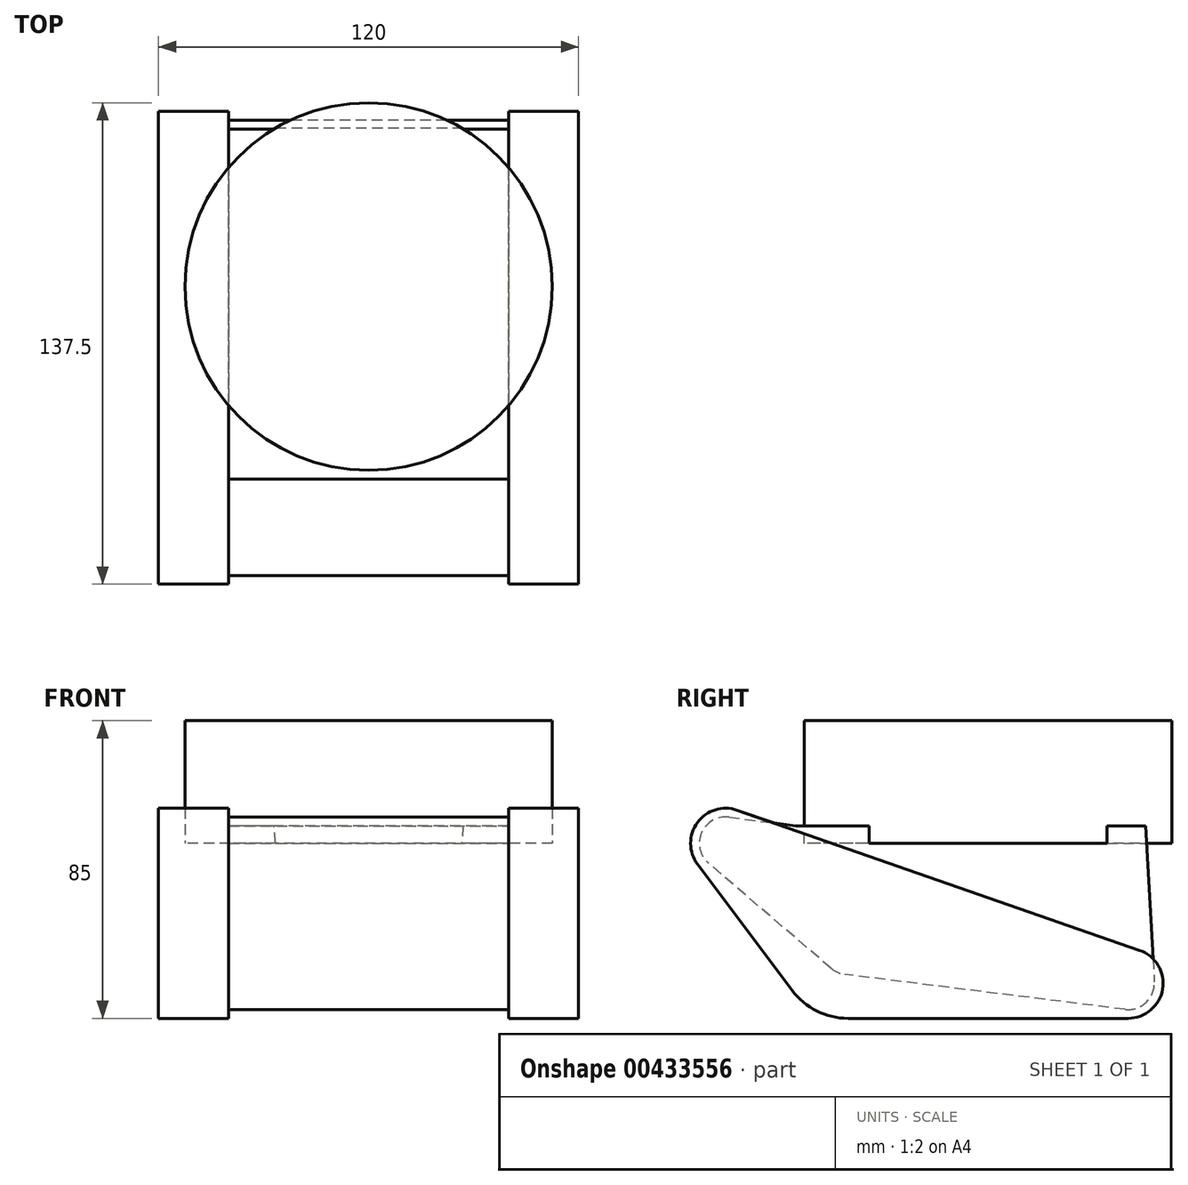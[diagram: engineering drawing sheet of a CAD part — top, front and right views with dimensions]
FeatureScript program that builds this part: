
annotation { "Feature Type Name" : "Feature", "Feature Type Description" : "" }
export const myFeature = defineFeature(function(context is Context, id is Id, definition is map)
    precondition{}
    {
        {
            var Q0;
            Q0=qCreatedBy(makeId("Right.planeOp"),FACE);
            var sketch = newSketch(context, id + "F0", { "sketchPlane" : qUnion([Q0])});
            skLineSegment(sketch, "E0", {"start": v(0, 0) * mm, "end": v(40, 0) * mm, "construction": true});
            skLineSegment(sketch, "E1", {"start": v(0, 0) * mm, "end": v(-40, 0) * mm, "construction": true});
            skLineSegment(sketch, "E2", {"start": v(-40, 0) * mm, "end": v(-40, 10) * mm, "construction": true});
            skCircle(sketch, "E3", {"center": v(40, 0) * mm, "radius": 10 * mm});
            skCircle(sketch, "E4", {"center": v(-40, 10) * mm, "radius": 20 * mm});
            skLineSegment(sketch, "E5", {"start": v(40, -10) * mm, "end": v(-40, -10) * mm});
            skLineSegment(sketch, "E6", {"start": v(-40, 0) * mm, "end": v(-75, 0) * mm, "construction": true});
            skLineSegment(sketch, "E7", {"start": v(-75, 0) * mm, "end": v(-75, 40) * mm, "construction": true});
            skCircle(sketch, "E8", {"center": v(-75, 40) * mm, "radius": 10 * mm});
            skLineSegment(sketch, "E9", {"start": v(-83, 34) * mm, "end": v(-56, -2) * mm});
            skLineSegment(sketch, "E10", {"start": v(-71.71, 49.44) * mm, "end": v(43.29, 9.44) * mm});
            skLineSegment(sketch, "E11", {"start": v(-40, 10) * mm, "end": v(-55, 10) * mm, "construction": true});
            skLineSegment(sketch, "E12", {"start": v(-55, 10) * mm, "end": v(-55, 45) * mm, "construction": true});
            skLineSegment(sketch, "E13", {"start": v(40, 0) * mm, "end": v(45, 0) * mm, "construction": true});
            skLineSegment(sketch, "E14", {"start": v(45, 0) * mm, "end": v(45, 45) * mm, "construction": true});
            skLineSegment(sketch, "E15.bottom", {"start": v(-55, 45) * mm, "end": v(45, 45) * mm});
            skLineSegment(sketch, "E15.top", {"start": v(-55, 75) * mm, "end": v(45, 75) * mm});
            skLineSegment(sketch, "E15.left", {"start": v(-55, 45) * mm, "end": v(-55, 75) * mm});
            skLineSegment(sketch, "E15.right", {"start": v(45, 45) * mm, "end": v(45, 75) * mm});
            skLineSegment(sketch, "E16", {"start": v(-5, 75) * mm, "end": v(-5, 45) * mm, "construction": true});
            skCircle(sketch, "E17", {"center": v(-75, 40) * mm, "radius": 7.5 * mm});
            skCircle(sketch, "E18", {"center": v(-40, 10) * mm, "radius": 7.5 * mm});
            skCircle(sketch, "E19", {"center": v(40, 0) * mm, "radius": 7.5 * mm});
            skLineSegment(sketch, "E20", {"start": v(39.07, -7.44) * mm, "end": v(-40.93, 2.56) * mm});
            skLineSegment(sketch, "E21", {"start": v(-44.88, 4.3) * mm, "end": v(-79.88, 34.3) * mm});
            skLineSegment(sketch, "E22", {"start": v(-74.05, 47.44) * mm, "end": v(-55, 45) * mm});
            skLineSegment(sketch, "E23", {"start": v(45, 45) * mm, "end": v(47.49, 0.42) * mm});
            skSolve(sketch);
        }
        {
            var Q0;
            {var subQ0=sQuery(id+"F0.wireOp",EDGE,"E17");var subQ1=makeQuery(id+"F0.imprint","INTERSECT",VERTEX,{"derivedFrom":[subQ0,sQuery(id+"F0.wireOp",EDGE,"E21")]});Q0=makeQuery(id+"F0.imprint","IMPRINT",FACE,{"disambiguationData":[TD([[makeQuery(id+"F0.imprint","IMPRINT",EDGE,{"disambiguationData":[TD([[subQ1,1.0]])],"derivedFrom":subQ0}),1.0]])]});}
            var Q1;
            {var subQ0=sQuery(id+"F0.wireOp",EDGE,"E10");var subQ1=sQuery(id+"F0.wireOp",EDGE,"E3");var subQ2=makeQuery(id+"F0.imprint","INTERSECT",VERTEX,{"derivedFrom":[subQ1,subQ0]});Q1=makeQuery(id+"F0.imprint","IMPRINT",FACE,{"disambiguationData":[TD([[makeQuery(id+"F0.imprint","IMPRINT",EDGE,{"disambiguationData":[TD([[subQ2,-1.0]])],"derivedFrom":subQ1}),-1.0]])]});}
            var Q2;
            {var subQ0=sQuery(id+"F0.wireOp",EDGE,"E22");var subQ1=sQuery(id+"F0.wireOp",EDGE,"E8");var subQ2=makeQuery(id+"F0.imprint","INTERSECT",VERTEX,{"derivedFrom":[subQ1,subQ0]});Q2=makeQuery(id+"F0.imprint","IMPRINT",FACE,{"disambiguationData":[TD([[makeQuery(id+"F0.imprint","IMPRINT",EDGE,{"disambiguationData":[TD([[subQ2,1.0]])],"derivedFrom":subQ1}),1.0]])]});}
            var Q3;
            {var subQ0=sQuery(id+"F0.wireOp",EDGE,"E21");var subQ1=sQuery(id+"F0.wireOp",EDGE,"E4");var subQ2=makeQuery(id+"F0.imprint","INTERSECT",VERTEX,{"derivedFrom":[subQ1,subQ0]});Q3=makeQuery(id+"F0.imprint","IMPRINT",FACE,{"disambiguationData":[TD([[makeQuery(id+"F0.imprint","IMPRINT",EDGE,{"disambiguationData":[TD([[subQ2,1.0]])],"derivedFrom":subQ1}),1.0]])]});}
            var Q4;
            {var subQ0=sQuery(id+"F0.wireOp",EDGE,"E18");var subQ1=makeQuery(id+"F0.imprint","INTERSECT",VERTEX,{"derivedFrom":[subQ0,sQuery(id+"F0.wireOp",EDGE,"E20")]});Q4=makeQuery(id+"F0.imprint","IMPRINT",FACE,{"disambiguationData":[TD([[makeQuery(id+"F0.imprint","IMPRINT",EDGE,{"disambiguationData":[TD([[subQ1,1.0]])],"derivedFrom":subQ0}),1.0]])]});}
            var Q5;
            {var subQ0=sQuery(id+"F0.wireOp",EDGE,"E19");var subQ1=makeQuery(id+"F0.imprint","INTERSECT",VERTEX,{"derivedFrom":[subQ0,sQuery(id+"F0.wireOp",EDGE,"E20")]});Q5=makeQuery(id+"F0.imprint","IMPRINT",FACE,{"disambiguationData":[TD([[makeQuery(id+"F0.imprint","IMPRINT",EDGE,{"disambiguationData":[TD([[subQ1,1.0]])],"derivedFrom":subQ0}),1.0]])]});}
            var Q6;
            {var subQ5=sQuery(id+"F0.wireOp",EDGE,"E3");var subQ7=makeQuery(id+"F0.imprint","INTERSECT",VERTEX,{"derivedFrom":[subQ5,sQuery(id+"F0.wireOp",EDGE,"E10")]});Q6=makeQuery(id+"F0.imprint","IMPRINT",FACE,{"disambiguationData":[TD([[makeQuery(id+"F0.imprint","IMPRINT",EDGE,{"disambiguationData":[TD([[subQ7,1.0]])],"derivedFrom":subQ5}),1.0]])]});}
            var Q7;
            {var subQ1=sQuery(id+"F0.wireOp",EDGE,"E15.bottom");Q7=makeQuery(id+"F0.imprint","IMPRINT",FACE,{"disambiguationData":[TD([[makeQuery(id+"F0.imprint","IMPRINT",EDGE,{"derivedFrom":subQ1}),-1.0]])]});}
            extrude(context, id + "F1", {"entities" : qUnion([Q0, Q1, Q2, Q3, Q4, Q5, Q6, Q7]), "depth" : 40 * mm});
        }
        {
            var Q0;
            {var subQ0=sQuery(id+"F0.wireOp",EDGE,"E8");var subQ8=makeQuery(id+"F0.imprint","INTERSECT",VERTEX,{"derivedFrom":[subQ0,sQuery(id+"F0.wireOp",EDGE,"E10")]});Q0=makeQuery(id+"F0.imprint","IMPRINT",FACE,{"disambiguationData":[TD([[makeQuery(id+"F0.imprint","IMPRINT",EDGE,{"disambiguationData":[TD([[subQ8,1.0]])],"derivedFrom":subQ0}),1.0]])]});}
            var Q1;
            {var subQ0=sQuery(id+"F0.wireOp",EDGE,"E10");var subQ1=sQuery(id+"F0.wireOp",EDGE,"E8");var subQ2=makeQuery(id+"F0.imprint","INTERSECT",VERTEX,{"derivedFrom":[subQ1,subQ0]});Q1=makeQuery(id+"F0.imprint","IMPRINT",FACE,{"disambiguationData":[TD([[makeQuery(id+"F0.imprint","IMPRINT",EDGE,{"disambiguationData":[TD([[subQ2,1.0]])],"derivedFrom":subQ1}),-1.0]])]});}
            var Q2;
            {var subQ0=sQuery(id+"F0.wireOp",EDGE,"E9");Q2=makeQuery(id+"F0.imprint","IMPRINT",FACE,{"disambiguationData":[TD([[makeQuery(id+"F0.imprint","IMPRINT",EDGE,{"derivedFrom":subQ0}),1.0]])]});}
            var Q3;
            {var subQ0=sQuery(id+"F0.wireOp",EDGE,"E17");var subQ1=makeQuery(id+"F0.imprint","INTERSECT",VERTEX,{"derivedFrom":[subQ0,sQuery(id+"F0.wireOp",EDGE,"E21")]});Q3=makeQuery(id+"F0.imprint","IMPRINT",FACE,{"disambiguationData":[TD([[makeQuery(id+"F0.imprint","IMPRINT",EDGE,{"disambiguationData":[TD([[subQ1,1.0]])],"derivedFrom":subQ0}),1.0]])]});}
            var Q4;
            {var subQ0=sQuery(id+"F0.wireOp",EDGE,"E22");var subQ1=sQuery(id+"F0.wireOp",EDGE,"E8");var subQ2=makeQuery(id+"F0.imprint","INTERSECT",VERTEX,{"derivedFrom":[subQ1,subQ0]});Q4=makeQuery(id+"F0.imprint","IMPRINT",FACE,{"disambiguationData":[TD([[makeQuery(id+"F0.imprint","IMPRINT",EDGE,{"disambiguationData":[TD([[subQ2,1.0]])],"derivedFrom":subQ1}),1.0]])]});}
            var Q5;
            {var subQ0=sQuery(id+"F0.wireOp",EDGE,"E10");var subQ1=sQuery(id+"F0.wireOp",EDGE,"E3");var subQ2=makeQuery(id+"F0.imprint","INTERSECT",VERTEX,{"derivedFrom":[subQ1,subQ0]});Q5=makeQuery(id+"F0.imprint","IMPRINT",FACE,{"disambiguationData":[TD([[makeQuery(id+"F0.imprint","IMPRINT",EDGE,{"disambiguationData":[TD([[subQ2,-1.0]])],"derivedFrom":subQ1}),-1.0]])]});}
            var Q6;
            {var subQ0=sQuery(id+"F0.wireOp",EDGE,"E18");var subQ1=makeQuery(id+"F0.imprint","INTERSECT",VERTEX,{"derivedFrom":[subQ0,sQuery(id+"F0.wireOp",EDGE,"E20")]});Q6=makeQuery(id+"F0.imprint","IMPRINT",FACE,{"disambiguationData":[TD([[makeQuery(id+"F0.imprint","IMPRINT",EDGE,{"disambiguationData":[TD([[subQ1,1.0]])],"derivedFrom":subQ0}),1.0]])]});}
            var Q7;
            {var subQ5=sQuery(id+"F0.wireOp",EDGE,"E4");var subQ8=makeQuery(id+"F0.imprint","INTERSECT",VERTEX,{"derivedFrom":[subQ5,sQuery(id+"F0.wireOp",EDGE,"E9")]});Q7=makeQuery(id+"F0.imprint","IMPRINT",FACE,{"disambiguationData":[TD([[makeQuery(id+"F0.imprint","IMPRINT",EDGE,{"disambiguationData":[TD([[subQ8,1.0]])],"derivedFrom":subQ5}),1.0]])]});}
            var Q8;
            {var subQ5=sQuery(id+"F0.wireOp",EDGE,"E3");var subQ7=makeQuery(id+"F0.imprint","INTERSECT",VERTEX,{"derivedFrom":[subQ5,sQuery(id+"F0.wireOp",EDGE,"E10")]});Q8=makeQuery(id+"F0.imprint","IMPRINT",FACE,{"disambiguationData":[TD([[makeQuery(id+"F0.imprint","IMPRINT",EDGE,{"disambiguationData":[TD([[subQ7,1.0]])],"derivedFrom":subQ5}),1.0]])]});}
            var Q9;
            {var subQ0=sQuery(id+"F0.wireOp",EDGE,"E19");var subQ1=makeQuery(id+"F0.imprint","INTERSECT",VERTEX,{"derivedFrom":[subQ0,sQuery(id+"F0.wireOp",EDGE,"E20")]});Q9=makeQuery(id+"F0.imprint","IMPRINT",FACE,{"disambiguationData":[TD([[makeQuery(id+"F0.imprint","IMPRINT",EDGE,{"disambiguationData":[TD([[subQ1,1.0]])],"derivedFrom":subQ0}),1.0]])]});}
            var Q10;
            {var subQ3=sQuery(id+"F0.wireOp",EDGE,"E3");var subQ7=makeQuery(id+"F0.imprint","INTERSECT",VERTEX,{"derivedFrom":[subQ3,sQuery(id+"F0.wireOp",EDGE,"E5")]});Q10=makeQuery(id+"F0.imprint","IMPRINT",FACE,{"disambiguationData":[TD([[makeQuery(id+"F0.imprint","IMPRINT",EDGE,{"disambiguationData":[TD([[subQ7,1.0]])],"derivedFrom":subQ3}),1.0]])]});}
            var Q11;
            {var subQ0=sQuery(id+"F0.wireOp",EDGE,"E5");Q11=makeQuery(id+"F0.imprint","IMPRINT",FACE,{"disambiguationData":[TD([[makeQuery(id+"F0.imprint","IMPRINT",EDGE,{"derivedFrom":subQ0}),-1.0]])]});}
            var Q12;
            {var subQ0=sQuery(id+"F0.wireOp",EDGE,"E21");var subQ1=sQuery(id+"F0.wireOp",EDGE,"E4");var subQ2=makeQuery(id+"F0.imprint","INTERSECT",VERTEX,{"derivedFrom":[subQ1,subQ0]});Q12=makeQuery(id+"F0.imprint","IMPRINT",FACE,{"disambiguationData":[TD([[makeQuery(id+"F0.imprint","IMPRINT",EDGE,{"disambiguationData":[TD([[subQ2,1.0]])],"derivedFrom":subQ1}),1.0]])]});}
            extrude(context, id + "F2", {"entities" : qUnion([Q0, Q1, Q2, Q3, Q4, Q5, Q6, Q7, Q8, Q9, Q10, Q11, Q12]), "depth" : 60 * mm, "hasSecondDirection" : true, "secondDirectionOppositeDirection" : false, "secondDirectionDepth" : 40 * mm});
        }
        {
            var Q0;
            Q0=makeQuery(id+"F2.opExtrude","SWEPT_BODY",BODY,{"disambiguationData":[OSD([sQuery(id+"F0.wireOp",EDGE,"E3"),sQuery(id+"F0.wireOp",EDGE,"E4"),sQuery(id+"F0.wireOp",EDGE,"E5"),sQuery(id+"F0.wireOp",EDGE,"E8"),sQuery(id+"F0.wireOp",EDGE,"E9"),sQuery(id+"F0.wireOp",EDGE,"E10")])]});
            var Q1;
            Q1=qCreatedBy(makeId("Right.planeOp"),FACE);
            mirror(context, id + "F3", {"entities" : qUnion([Q0]), "mirrorPlane" : qUnion([Q1])});
        }
        {
            var Q0;
            Q0=makeQuery(id+"F1.opExtrude","SWEPT_BODY",BODY,{"disambiguationData":[OSD([sQuery(id+"F0.wireOp",EDGE,"E15.bottom"),sQuery(id+"F0.wireOp",EDGE,"E17"),sQuery(id+"F0.wireOp",EDGE,"E18"),sQuery(id+"F0.wireOp",EDGE,"E19"),sQuery(id+"F0.wireOp",EDGE,"E20"),sQuery(id+"F0.wireOp",EDGE,"E21"),sQuery(id+"F0.wireOp",EDGE,"E22"),sQuery(id+"F0.wireOp",EDGE,"E23")])]});
            var Q1;
            Q1=qCreatedBy(makeId("Right.planeOp"),FACE);
            mirror(context, id + "F4", {"operationType" : NewBodyOperationType.ADD, "entities" : qUnion([Q0]), "mirrorPlane" : qUnion([Q1])});
        }
        {
            var Q0;
            {var subQ0=makeQuery(id+"F1.opExtrude","SWEPT_FACE",FACE,{"disambiguationData":[OSD([sQuery(id+"F0.wireOp",EDGE,"E15.bottom")])]});Q0=makeQuery(id+"F3.boolean.opBoolean","MERGE",FACE,{"derivedFrom":[subQ0,makeQuery(id+"F3.opPattern","COPY",FACE,{"derivedFrom":subQ0,"instanceName":"1"})]});}
            var sketch = newSketch(context, id + "F5", { "sketchPlane" : qUnion([Q0])});
            skCircle(sketch, "E24", {"center": v(0, 0) * mm, "radius": 52.5 * mm});
            skSolve(sketch);
        }
        {
            var Q0;
            {var subQ0=sQuery(id+"F5.wireOp",EDGE,"E24");var subQ1=sQuery(id+"F0.wireOp",EDGE,"E15.bottom");var subQ2=makeQuery(id+"F1.opExtrude","CAP_EDGE",EDGE,{"disambiguationData":[OSD([subQ1])],"isStart":false});var subQ5=makeQuery(id+"F4.opPattern","COPY",EDGE,{"derivedFrom":subQ2,"instanceName":"1"});var subQ6=makeQuery(id+"F5.imprint","INTERSECT",VERTEX,{"disambiguationData":[OD(1.0)],"derivedFrom":[subQ5,subQ0]});Q0=makeQuery(id+"F5.imprint","IMPRINT",FACE,{"disambiguationData":[TD([[makeQuery(id+"F5.imprint","IMPRINT",EDGE,{"disambiguationData":[TD([[subQ6,-1.0]])],"derivedFrom":subQ0}),1.0]])]});}
            var Q1;
            {var subQ0=sQuery(id+"F5.wireOp",EDGE,"E24");var subQ1=makeQuery(id+"F1.opExtrude","SWEPT_EDGE",EDGE,{"disambiguationData":[OSD([sQuery(id+"F0.wireOp",EDGE,"E15.bottom"),sQuery(id+"F0.wireOp",EDGE,"E15.right"),sQuery(id+"F0.wireOp",EDGE,"E23")])]});var subQ2=makeQuery(id+"F4.boolean.opBoolean","MERGE",EDGE,{"derivedFrom":[subQ1,makeQuery(id+"F4.opPattern","COPY",EDGE,{"derivedFrom":subQ1,"instanceName":"1"})]});var subQ3=makeQuery(id+"F5.imprint","INTERSECT",VERTEX,{"disambiguationData":[OD(0.0)],"derivedFrom":[subQ2,subQ0]});Q1=makeQuery(id+"F5.imprint","IMPRINT",FACE,{"disambiguationData":[TD([[makeQuery(id+"F5.imprint","IMPRINT",EDGE,{"disambiguationData":[TD([[subQ3,-1.0]])],"derivedFrom":subQ0}),1.0]])]});}
            extrude(context, id + "F6", {"entities" : qUnion([Q0, Q1]), "operationType" : NewBodyOperationType.REMOVE, "oppositeDirection" : true, "depth" : 5 * mm});
        }
        {
            var Q0;
            {var subQ0=sQuery(id+"F5.wireOp",EDGE,"E24");var subQ1=makeQuery(id+"F4.opPattern","COPY",EDGE,{"derivedFrom":makeQuery(id+"F1.opExtrude","CAP_EDGE",EDGE,{"disambiguationData":[OSD([sQuery(id+"F0.wireOp",EDGE,"E15.bottom")])],"isStart":false}),"instanceName":"1"});var subQ2=makeQuery(id+"F5.imprint","INTERSECT",VERTEX,{"disambiguationData":[OD(0.0)],"derivedFrom":[subQ1,subQ0]});Q0=makeQuery(id+"F5.imprint","IMPRINT",FACE,{"disambiguationData":[TD([[makeQuery(id+"F5.imprint","IMPRINT",EDGE,{"disambiguationData":[TD([[subQ2,-1.0]])],"derivedFrom":subQ0}),1.0]])]});}
            var Q1;
            {var subQ0=sQuery(id+"F5.wireOp",EDGE,"E24");var subQ1=makeQuery(id+"F1.opExtrude","SWEPT_EDGE",EDGE,{"disambiguationData":[OSD([sQuery(id+"F0.wireOp",EDGE,"E15.bottom"),sQuery(id+"F0.wireOp",EDGE,"E15.right"),sQuery(id+"F0.wireOp",EDGE,"E23")])]});var subQ2=makeQuery(id+"F4.boolean.opBoolean","MERGE",EDGE,{"derivedFrom":[subQ1,makeQuery(id+"F4.opPattern","COPY",EDGE,{"derivedFrom":subQ1,"instanceName":"1"})]});var subQ3=makeQuery(id+"F5.imprint","INTERSECT",VERTEX,{"disambiguationData":[OD(0.0)],"derivedFrom":[subQ2,subQ0]});Q1=makeQuery(id+"F5.imprint","IMPRINT",FACE,{"disambiguationData":[TD([[makeQuery(id+"F5.imprint","IMPRINT",EDGE,{"disambiguationData":[TD([[subQ3,-1.0]])],"derivedFrom":subQ0}),1.0]])]});}
            var Q2;
            {var subQ0=sQuery(id+"F5.wireOp",EDGE,"E24");var subQ1=makeQuery(id+"F1.opExtrude","CAP_EDGE",EDGE,{"disambiguationData":[OSD([sQuery(id+"F0.wireOp",EDGE,"E15.bottom")])],"isStart":false});var subQ2=makeQuery(id+"F5.imprint","INTERSECT",VERTEX,{"disambiguationData":[OD(0.0)],"derivedFrom":[subQ1,subQ0]});Q2=makeQuery(id+"F5.imprint","IMPRINT",FACE,{"disambiguationData":[TD([[makeQuery(id+"F5.imprint","IMPRINT",EDGE,{"disambiguationData":[TD([[subQ2,1.0]])],"derivedFrom":subQ0}),1.0]])]});}
            var Q3;
            {var subQ0=sQuery(id+"F5.wireOp",EDGE,"E24");var subQ1=sQuery(id+"F0.wireOp",EDGE,"E15.bottom");var subQ2=makeQuery(id+"F1.opExtrude","CAP_EDGE",EDGE,{"disambiguationData":[OSD([subQ1])],"isStart":false});var subQ5=makeQuery(id+"F4.opPattern","COPY",EDGE,{"derivedFrom":subQ2,"instanceName":"1"});var subQ6=makeQuery(id+"F5.imprint","INTERSECT",VERTEX,{"disambiguationData":[OD(1.0)],"derivedFrom":[subQ5,subQ0]});Q3=makeQuery(id+"F5.imprint","IMPRINT",FACE,{"disambiguationData":[TD([[makeQuery(id+"F5.imprint","IMPRINT",EDGE,{"disambiguationData":[TD([[subQ6,-1.0]])],"derivedFrom":subQ0}),1.0]])]});}
            extrude(context, id + "F7", {"entities" : qUnion([Q0, Q1, Q2, Q3]), "depth" : 30 * mm, "hasSecondDirection" : true, "secondDirectionOppositeDirection" : true, "secondDirectionDepth" : 5 * mm});
        }
    });
